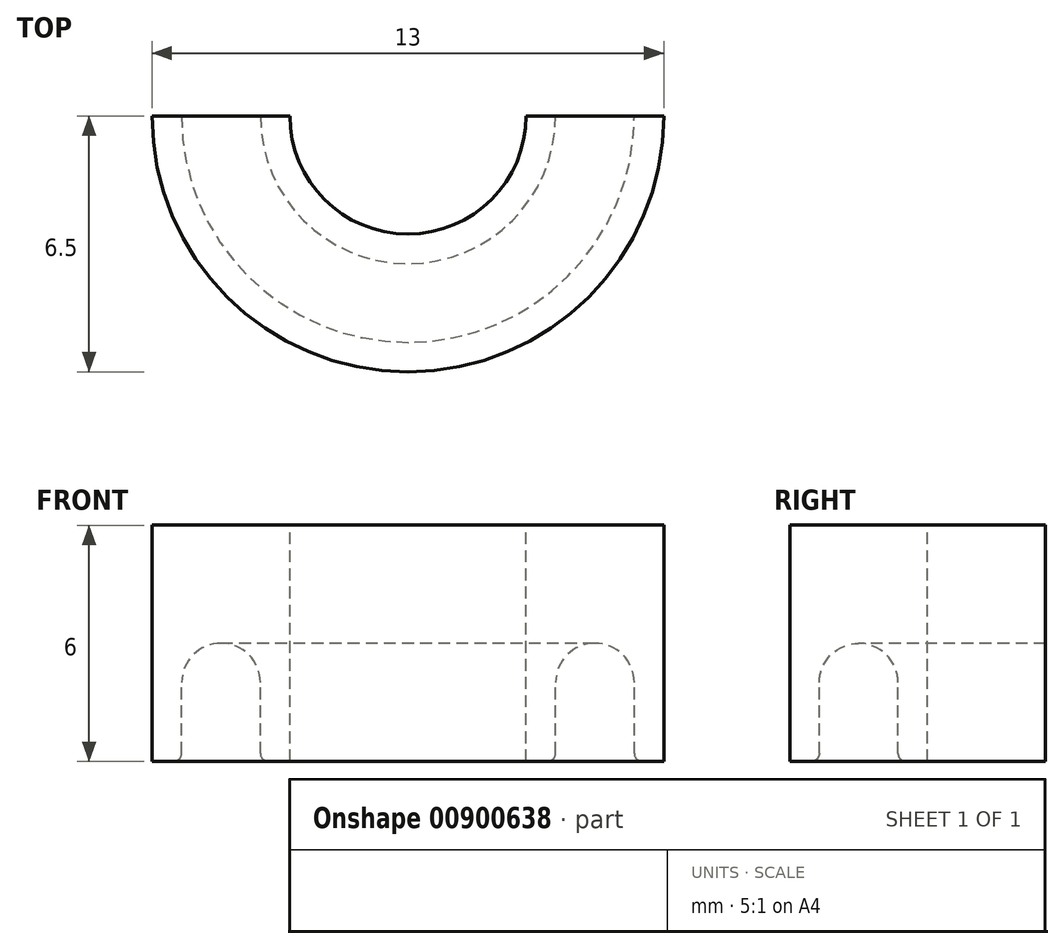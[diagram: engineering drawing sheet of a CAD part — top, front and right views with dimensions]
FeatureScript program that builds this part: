
annotation { "Feature Type Name" : "Feature", "Feature Type Description" : "" }
export const myFeature = defineFeature(function(context is Context, id is Id, definition is map)
    precondition{}
    {
        {
            var Q0;
            Q0=qCreatedBy(makeId("Front.planeOp"),FACE);
            var sketch = newSketch(context, id + "F0", { "sketchPlane" : qUnion([Q0])});
            skLineSegment(sketch, "E0.bottom", {"start": v(3, 2.28) * mm, "end": v(6.5, 2.28) * mm});
            skLineSegment(sketch, "E0.top", {"start": v(3, -3.72) * mm, "end": v(3.75, -3.72) * mm});
            skLineSegment(sketch, "E0.left", {"start": v(3, 2.28) * mm, "end": v(3, -3.72) * mm});
            skLineSegment(sketch, "E0.right", {"start": v(6.5, 2.28) * mm, "end": v(6.5, -3.72) * mm});
            skLineSegment(sketch, "E1.left", {"start": v(3.75, -3.72) * mm, "end": v(3.75, -1.72) * mm});
            skLineSegment(sketch, "E1.right", {"start": v(5.75, -3.72) * mm, "end": v(5.75, -1.72) * mm});
            skLineSegment(sketch, "E2.trimOffspring", {"start": v(5.75, -3.72) * mm, "end": v(6.5, -3.72) * mm});
            skLineSegment(sketch, "E3", {"start": v(0, 5.67) * mm, "end": v(0, -5.8) * mm, "construction": true});
            skLineSegment(sketch, "E4", {"start": v(0, -5.8) * mm, "end": v(0, 3.76) * mm, "construction": true});
            skArc(sketch, "E5", {"start": v(5.75, -1.72) * mm, "mid": v(4.75, -0.72) * mm, "end": v(3.75, -1.72) * mm});
            skSolve(sketch);
        }
        {
            var Q0;
            Q0=makeQuery(id+"F0.imprint","IMPRINT",FACE,{"disambiguationData":[TD([[makeQuery(id+"F0.imprint","IMPRINT",EDGE,{"derivedFrom":sQuery(id+"F0.wireOp",EDGE,"E0.bottom")}),-1.0]])]});
            var Q1;
            Q1=sQuery(id+"F0.wireOp",EDGE,"E3");
            revolve(context, id + "F1", {"surfaceOperationType" : NewSurfaceOperationType.NEW, "entities" : qUnion([Q0]), "axis" : qUnion([Q1]), "revolveType" : RevolveType.FULL});
        }
        {
            var Q0;
            Q0=makeQuery(id+"F1.opRevolve","SWEPT_EDGE",EDGE,{"disambiguationData":[OSD([sQuery(id+"F0.wireOp",EDGE,"E1.right"),sQuery(id+"F0.wireOp",EDGE,"E2.trimOffspring")])]});
            var Q1;
            Q1=makeQuery(id+"F1.opRevolve","SWEPT_EDGE",EDGE,{"disambiguationData":[OSD([sQuery(id+"F0.wireOp",EDGE,"E0.top"),sQuery(id+"F0.wireOp",EDGE,"E1.left")])]});
            fillet(context, id + "F2", {"entities" : qUnion([Q0, Q1]), "radius" : 0.2 * mm, "tangentPropagation" : true, "allowEdgeOverflow" : false});
        }
        {
            var Q0;
            Q0=qCreatedBy(makeId("Front.planeOp"),FACE);
            var sketch = newSketch(context, id + "F3", { "sketchPlane" : qUnion([Q0])});
            skLineSegment(sketch, "E6.bottom", {"start": v(-14.8, 15.51) * mm, "end": v(20.71, 15.51) * mm});
            skLineSegment(sketch, "E6.top", {"start": v(-14.8, -15.3) * mm, "end": v(20.71, -15.3) * mm});
            skLineSegment(sketch, "E6.left", {"start": v(-14.8, 15.51) * mm, "end": v(-14.8, -15.3) * mm});
            skLineSegment(sketch, "E6.right", {"start": v(20.71, 15.51) * mm, "end": v(20.71, -15.3) * mm});
            skSolve(sketch);
        }
        {
            var Q0;
            Q0=makeQuery(id+"F3.imprint","IMPRINT",FACE,{"disambiguationData":[TD([[makeQuery(id+"F3.imprint","IMPRINT",EDGE,{"derivedFrom":sQuery(id+"F3.wireOp",EDGE,"E6.bottom")}),-1.0]])]});
            extrude(context, id + "F4", {"entities" : qUnion([Q0]), "operationType" : NewBodyOperationType.REMOVE, "oppositeDirection" : true, "depth" : 25 * mm, "offsetDistance" : 25 * mm});
        }
    });
